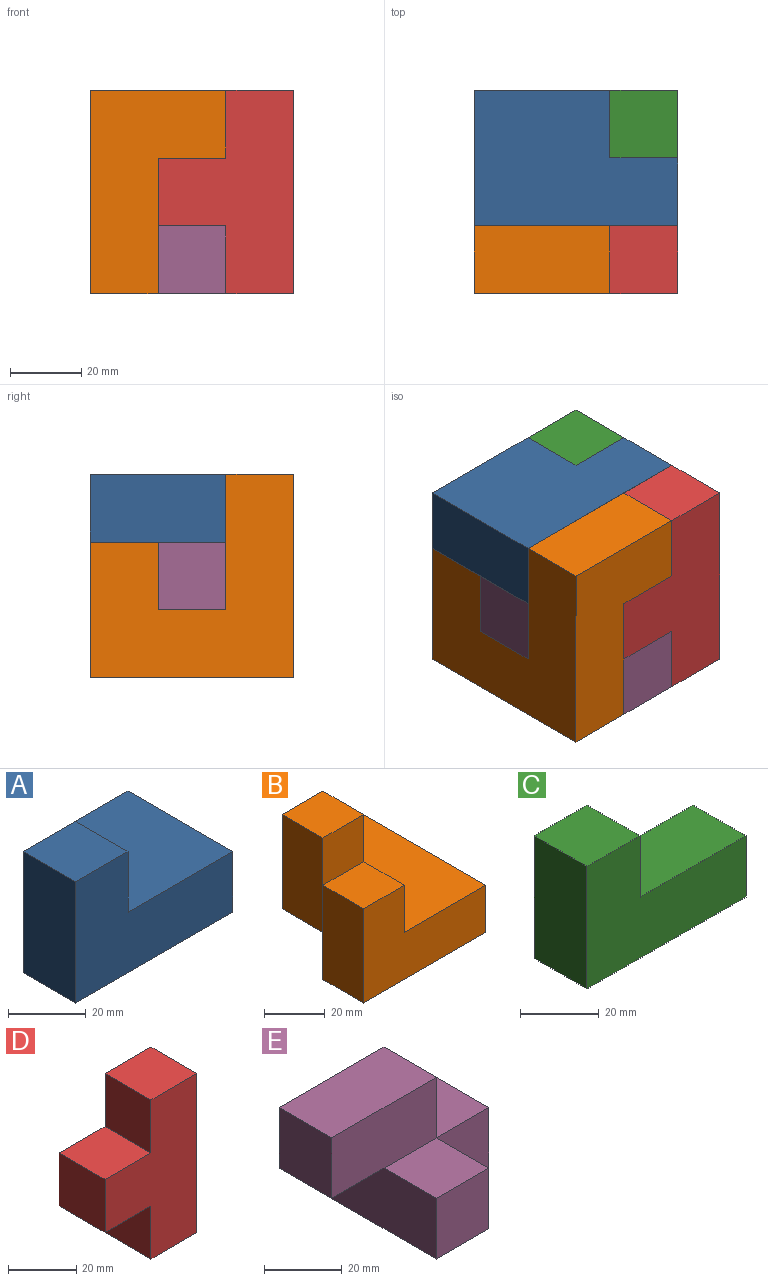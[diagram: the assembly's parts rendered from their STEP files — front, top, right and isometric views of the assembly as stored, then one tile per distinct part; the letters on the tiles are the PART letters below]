
ASSEMBLY  parts=5 mates=12
PART A: 10 faces, bbox 57.2x38.1x38.1 mm
  f0: plane 38.1x19.05mm, normal (-1,0,0), area 725.8mm2, adj f1,f5,f6,f7
  f1: plane 57.15x38.1mm, normal (0,0,-1), area 1814.5mm2, adj f0,f2,f6,f7,f8,f9
  f2: plane 38.1x19.05mm, normal (1,0,0), area 725.8mm2, adj f1,f3,f6,f9
  f3: plane 38.1x38.1mm, normal (0,0,1), area 1451.6mm2, adj f2,f4,f6,f8,f9
  f4: plane 19.05x19.05mm, normal (1,0,0), area 362.9mm2, adj f3,f5,f6,f7
  f5: plane 19.05x19.05mm, normal (0,0,1), area 362.9mm2, adj f0,f4,f6,f7
  f6: plane 57.15x38.1mm, normal (0,-1,0), area 1451.6mm2, adj f0,f1,f2,f3,f4,f5
  f7: plane 38.1x19.05mm, normal (0,1,0), area 725.8mm2, adj f0,f1,f4,f5,f8
  f8: plane 19.05x19.05mm, normal (-1,0,0), area 362.9mm2, adj f1,f3,f7,f9
  f9: plane 38.1x19.05mm, normal (0,1,0), area 725.8mm2, adj f1,f2,f3,f8
PART B: 14 faces, bbox 57.2x57.2x38.1 mm
  f0: plane 57.15x38.1mm, normal (0,0,1), area 1451.6mm2, adj f1,f4,f5,f7,f8,f9,f12
  f1: plane 19.05x19.05mm, normal (-1,0,0), area 362.9mm2, adj f0,f3,f8,f10
  f2: plane 38.1x19.05mm, normal (-1,0,0), area 725.8mm2, adj f3,f6,f7,f8
  f3: plane 57.15x57.15mm, normal (0,0,-1), area 2177.4mm2, adj f1,f2,f4,f7,f8,f9,f10,f11
  f4: plane 57.15x19.05mm, normal (1,0,0), area 1088.7mm2, adj f0,f3,f7,f9
  f5: plane 19.05x19.05mm, normal (1,0,0), area 362.9mm2, adj f0,f6,f7,f8
  f6: plane 19.05x19.05mm, normal (0,0,1), area 362.9mm2, adj f2,f5,f7,f8
  f7: plane 57.15x38.1mm, normal (0,-1,0), area 1451.6mm2, adj f0,f2,f3,f4,f5,f6
  f8: plane 38.1x38.1mm, normal (0,1,0), area 1088.7mm2, adj f0,f1,f2,f3,f5,f6
  f9: plane 38.1x38.1mm, normal (0,1,0), area 1088.7mm2, adj f0,f3,f4,f11,f12,f13
  f10: plane 38.1x19.05mm, normal (0,-1,0), area 725.8mm2, adj f1,f3,f11,f12,f13
  f11: plane 38.1x19.05mm, normal (-1,0,0), area 725.8mm2, adj f3,f9,f10,f13
  f12: plane 19.05x19.05mm, normal (1,0,0), area 362.9mm2, adj f0,f9,f10,f13
  f13: plane 19.05x19.05mm, normal (0,0,1), area 362.9mm2, adj f9,f10,f11,f12
PART C: 8 faces, bbox 57.2x19.1x38.1 mm
  f0: plane 38.1x19.05mm, normal (-1,0,0), area 725.8mm2, adj f1,f5,f6,f7
  f1: plane 57.15x19.05mm, normal (0,0,-1), area 1088.7mm2, adj f0,f2,f6,f7
  f2: plane 19.05x19.05mm, normal (1,0,0), area 362.9mm2, adj f1,f3,f6,f7
  f3: plane 38.1x19.05mm, normal (0,0,1), area 725.8mm2, adj f2,f4,f6,f7
  f4: plane 19.05x19.05mm, normal (1,0,0), area 362.9mm2, adj f3,f5,f6,f7
  f5: plane 19.05x19.05mm, normal (0,0,1), area 362.9mm2, adj f0,f4,f6,f7
  f6: plane 57.15x38.1mm, normal (0,-1,0), area 1451.6mm2, adj f0,f1,f2,f3,f4,f5
  f7: plane 57.15x38.1mm, normal (0,1,0), area 1451.6mm2, adj f0,f1,f2,f3,f4,f5
PART D: 10 faces, bbox 38.1x19.1x57.2 mm
  f0: plane 19.05x19.05mm, normal (0,0,-1), area 362.9mm2, adj f1,f7,f8,f9
  f1: plane 19.05x19.05mm, normal (-1,0,0), area 362.9mm2, adj f0,f2,f8,f9
  f2: plane 19.05x19.05mm, normal (0,0,-1), area 362.9mm2, adj f1,f3,f8,f9
  f3: plane 57.15x19.05mm, normal (1,0,0), area 1088.7mm2, adj f2,f4,f8,f9
  f4: plane 19.05x19.05mm, normal (0,0,1), area 362.9mm2, adj f3,f5,f8,f9
  f5: plane 19.05x19.05mm, normal (-1,0,0), area 362.9mm2, adj f4,f6,f8,f9
  f6: plane 19.05x19.05mm, normal (0,0,1), area 362.9mm2, adj f5,f7,f8,f9
  f7: plane 19.05x19.05mm, normal (-1,0,0), area 362.9mm2, adj f0,f6,f8,f9
  f8: plane 57.15x38.1mm, normal (0,-1,0), area 1451.6mm2, adj f0,f1,f2,f3,f4,f5,f6,f7
  f9: plane 57.15x38.1mm, normal (0,1,0), area 1451.6mm2, adj f0,f1,f2,f3,f4,f5,f6,f7
PART E: 14 faces, bbox 57.2x38.1x38.1 mm
  f0: plane 19.05x19.05mm, normal (0,-1,0), area 362.9mm2, adj f3,f4,f5,f11
  f1: plane 38.1x19.05mm, normal (0,-1,0), area 725.8mm2, adj f6,f7,f8,f9,f12
  f2: plane 38.1x19.05mm, normal (-1,0,0), area 725.8mm2, adj f3,f9,f10,f12,f13
  f3: plane 38.1x38.1mm, normal (0,0,-1), area 1088.7mm2, adj f0,f2,f4,f10,f11,f13
  f4: plane 19.05x19.05mm, normal (1,0,0), area 362.9mm2, adj f0,f3,f5,f10
  f5: plane 19.05x19.05mm, normal (0,0,1), area 362.9mm2, adj f0,f4,f6,f10
  f6: plane 19.05x19.05mm, normal (1,0,0), area 362.9mm2, adj f1,f5,f7,f10
  f7: plane 38.1x19.05mm, normal (0,0,1), area 725.8mm2, adj f1,f6,f8,f10
  f8: plane 19.05x19.05mm, normal (-1,0,0), area 362.9mm2, adj f1,f7,f9,f10
  f9: plane 19.05x19.05mm, normal (0,0,-1), area 362.9mm2, adj f1,f2,f8,f10
  f10: plane 57.15x38.1mm, normal (0,1,0), area 1451.6mm2, adj f2,f3,f4,f5,f6,f7,f8,f9
  f11: plane 19.05x19.05mm, normal (1,0,0), area 362.9mm2, adj f0,f3,f12,f13
  f12: plane 19.05x19.05mm, normal (0,0,1), area 362.9mm2, adj f1,f2,f11,f13
  f13: plane 19.05x19.05mm, normal (0,-1,0), area 362.9mm2, adj f2,f3,f11,f12
PLACE A rot(axis=(0,-1,0),180deg) t=(-75.47,-77.88,47.02)mm
PLACE B rot(axis=(0,1,0),90deg) t=(-88.17,-96.93,40.67)mm
PLACE C rot(axis=(0,-1,0),90deg) t=(-50.07,-58.83,8.92)mm
PLACE D rot(axis=(0.9,0.31,-0.31),0deg) t=(-69.12,-96.93,27.97)mm
PLACE E rot(axis=(0.9,0.31,-0.31),0deg) t=(-88.17,-77.88,8.92)mm
MATE planar E.f7 <-> B.f11  axis (0,0,1) through (-88.17,-77.88,47.02)mm
MATE planar A.f9 <-> C.f7  axis (0,1,0) through (-88.17,-58.83,56.54)mm
MATE planar A.f0 <-> D.f3  axis (1,0,0) through (-50.07,-87.41,47.02)mm
MATE planar B.f4 <-> C.f0  axis (0,0,-1) through (-97.7,-87.41,8.92)mm
MATE planar B.f9 <-> C.f7  axis (0,1,0) through (-91.35,-58.83,31.14)mm
MATE planar D.f8 <-> B.f7  axis (0,-1,0) through (-64.36,-115.98,37.49)mm
MATE planar E.f4 <-> C.f1  axis (1,0,0) through (-50.07,-87.41,18.44)mm
MATE planar D.f3 <-> C.f1  axis (1,0,0) through (-50.07,-106.46,37.49)mm
MATE planar B.f7 <-> E.f13  axis (0,-1,0) through (-92.93,-115.98,42.26)mm
MATE planar B.f3 <-> E.f8  axis (-1,0,0) through (-107.22,-96.93,27.97)mm
MATE planar A.f1 <-> C.f2  axis (0,0,1) through (-82.46,-79.79,66.07)mm
MATE planar B.f2 <-> D.f4  axis (0,0,1) through (-88.17,-106.46,66.07)mm
